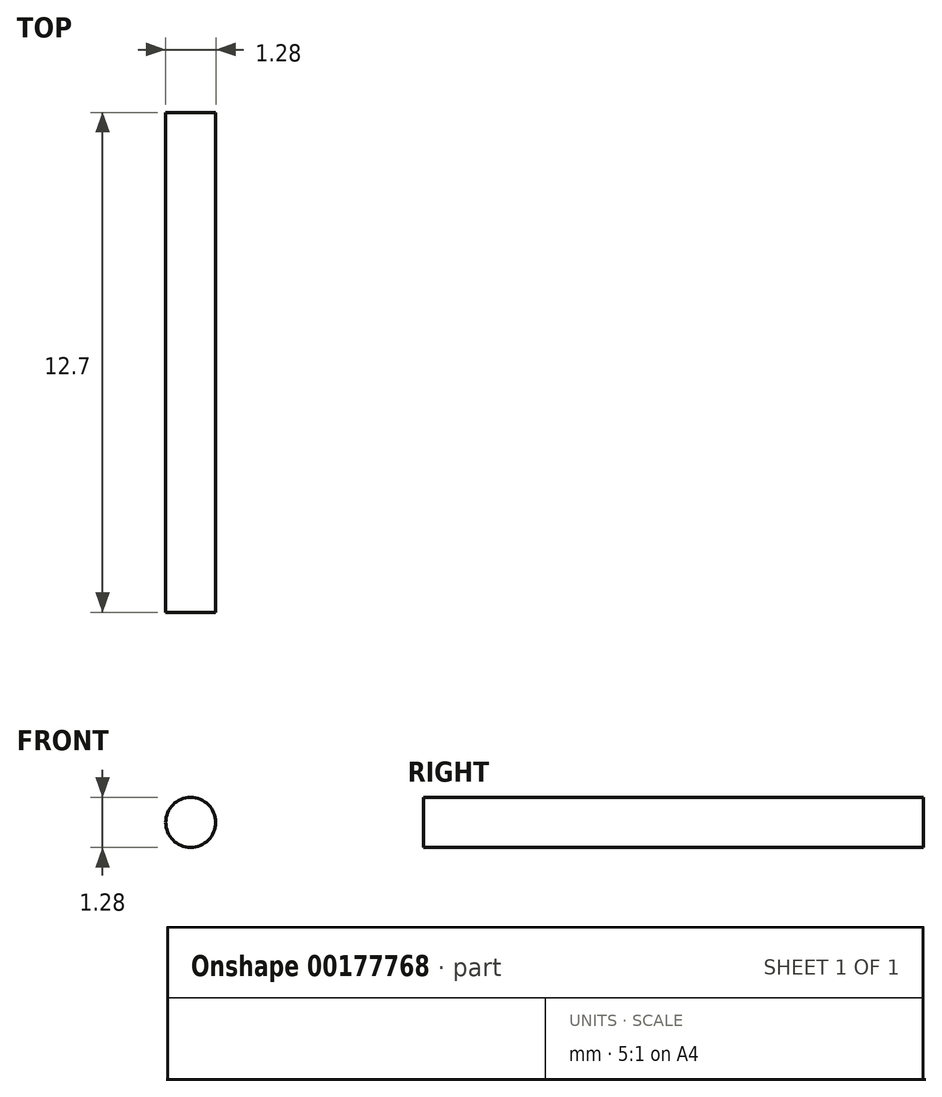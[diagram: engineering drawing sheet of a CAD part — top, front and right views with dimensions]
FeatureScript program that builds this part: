
annotation { "Feature Type Name" : "Feature", "Feature Type Description" : "" }
export const myFeature = defineFeature(function(context is Context, id is Id, definition is map)
    precondition{}
    {
        {
            var Q0;
            Q0=qCreatedBy(makeId("Front.planeOp"),FACE);
            var sketch = newSketch(context, id + "F0", { "sketchPlane" : qUnion([Q0])});
            skCircle(sketch, "E0", {"center": v(0, 0) * mm, "radius": 0.64 * mm});
            skSolve(sketch);
        }
        {
            var Q0;
            Q0 = qSketchRegion(id + "F0", true);
            extrude(context, id + "F1", {"entities" : qUnion([Q0]), "endBound" : BoundingType.SYMMETRIC, "depth" : 12.7 * mm});
        }
    });
